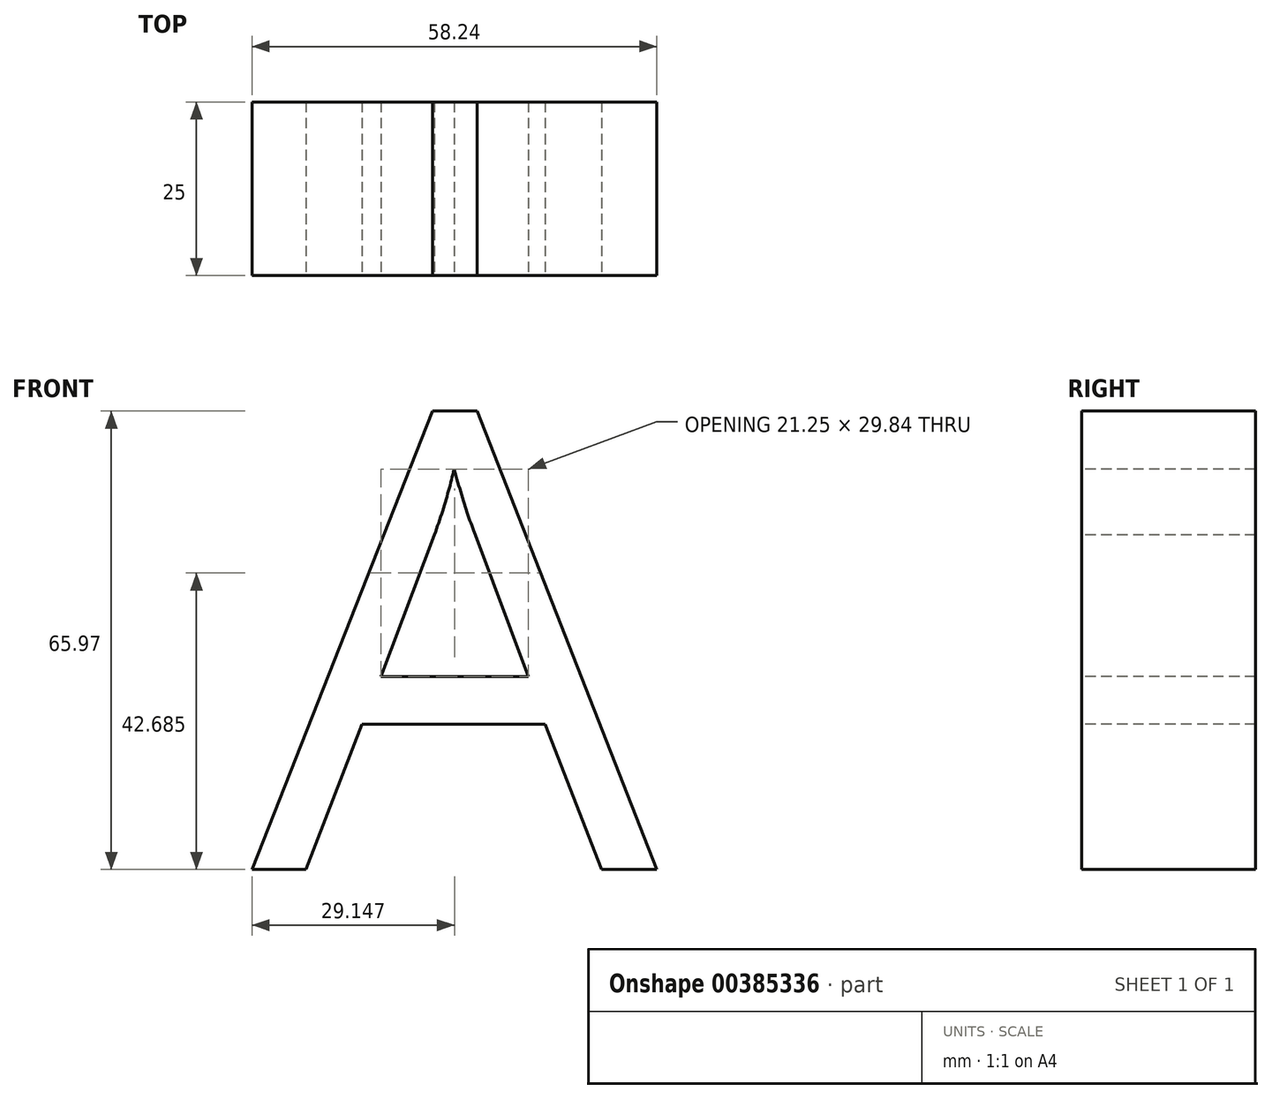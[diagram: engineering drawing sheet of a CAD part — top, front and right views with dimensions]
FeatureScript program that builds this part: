
annotation { "Feature Type Name" : "Feature", "Feature Type Description" : "" }
export const myFeature = defineFeature(function(context is Context, id is Id, definition is map)
    precondition{}
    {
        {
            var Q0;
            Q0=qCreatedBy(makeId("Front.planeOp"),FACE);
            var sketch = newSketch(context, id + "F0", { "sketchPlane" : qUnion([Q0])});
            skText(sketch, "E0", { "text": "A", "fontName": "OpenSans-Regular.ttf"});
            const initialGuessF0  = {"E0": [-0.0436, -0.02523, 1, 0, 0.06626]};
            skSetInitialGuess(sketch, initialGuessF0);
            skSolve(sketch);
        }
        {
            var Q0;
            Q0 = qSketchRegion(id + "F0", true);
            extrude(context, id + "F1", {"entities" : qUnion([Q0]), "oppositeDirection" : true, "depth" : 25 * mm});
        }
    });
